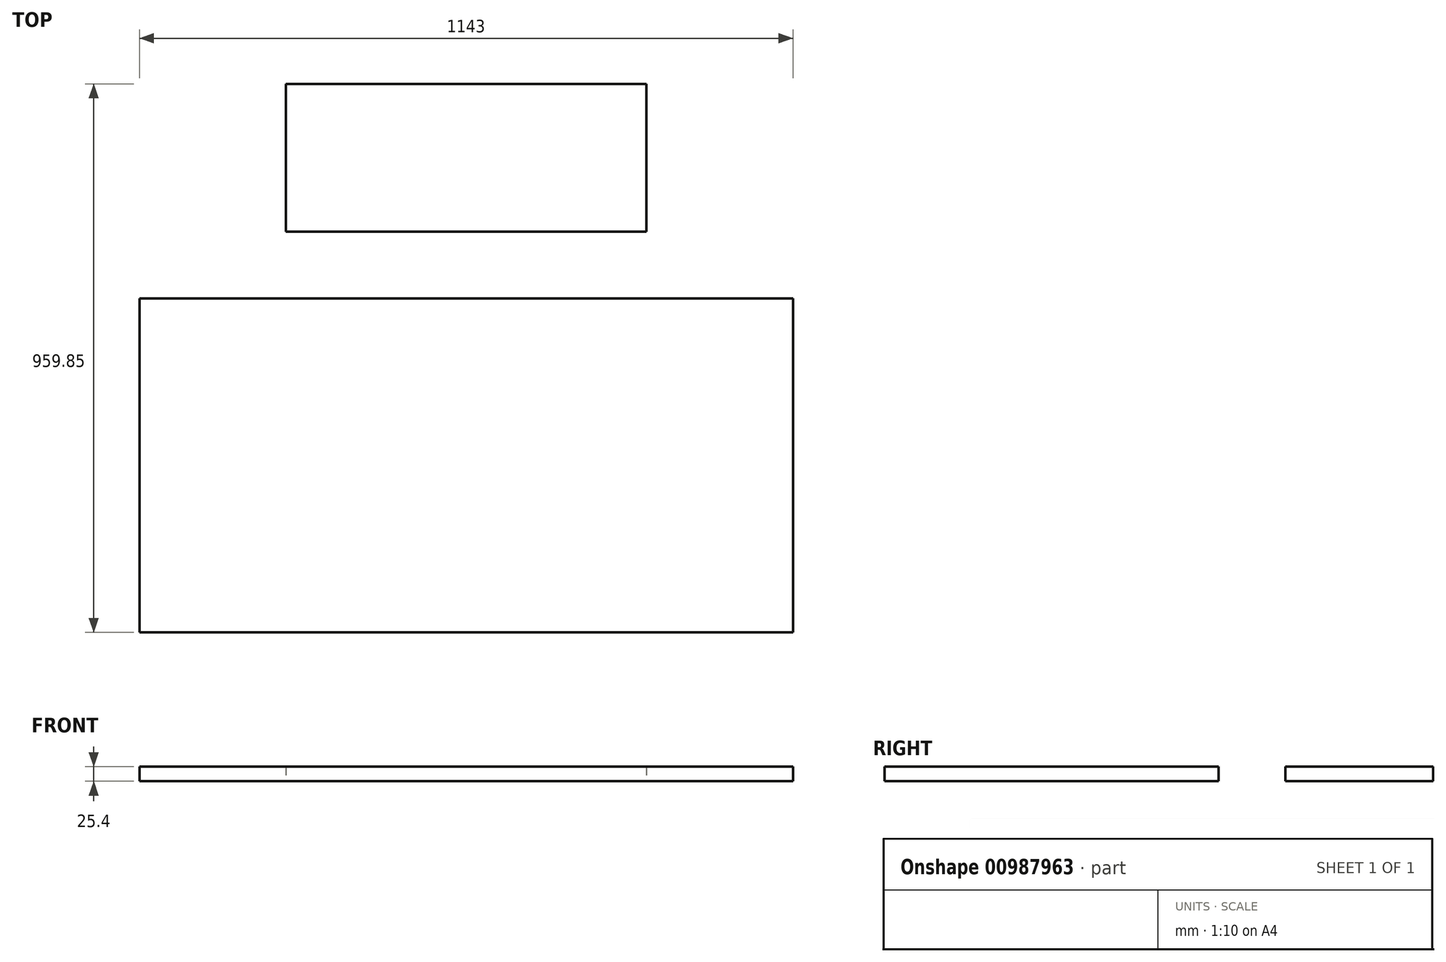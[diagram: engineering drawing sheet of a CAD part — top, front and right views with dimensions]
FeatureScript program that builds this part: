
annotation { "Feature Type Name" : "Feature", "Feature Type Description" : "" }
export const myFeature = defineFeature(function(context is Context, id is Id, definition is map)
    precondition{}
    {
        {
            var Q0;
            Q0=qCreatedBy(makeId("Top.planeOp"),FACE);
            var sketch = newSketch(context, id + "F0", { "sketchPlane" : qUnion([Q0])});
            skLineSegment(sketch, "E0.bottom", {"start": v(0, -44.7) * mm, "end": v(1143, -44.7) * mm});
            skLineSegment(sketch, "E0.top", {"start": v(0, 539.5) * mm, "end": v(1143, 539.5) * mm});
            skLineSegment(sketch, "E0.left", {"start": v(0, -44.7) * mm, "end": v(0, 539.5) * mm});
            skLineSegment(sketch, "E0.right", {"start": v(1143, -44.7) * mm, "end": v(1143, 539.5) * mm});
            skLineSegment(sketch, "E1.bottom", {"start": v(886.92, 915.14) * mm, "end": v(256.08, 915.14) * mm});
            skLineSegment(sketch, "E1.top", {"start": v(886.92, 656.58) * mm, "end": v(256.08, 656.58) * mm});
            skLineSegment(sketch, "E1.left", {"start": v(886.92, 915.14) * mm, "end": v(886.92, 656.58) * mm});
            skLineSegment(sketch, "E1.right", {"start": v(256.08, 915.14) * mm, "end": v(256.08, 656.58) * mm});
            skPoint(sketch, "E1.middle", {"position": v(571.5, 785.86) * mm});
            skPoint(sketch, "E1.middle.positionSnap0", {"position": v(571.5, 539.5) * mm});
            skPoint(sketch, "E1.centerSnap0", {"position": v(571.5, 539.5) * mm});
            skSolve(sketch);
        }
        {
            var Q0;
            Q0 = qSketchRegion(id + "F0", true);
            extrude(context, id + "F1", {"entities" : qUnion([Q0]), "depth" : 25.4 * mm, "offsetDistance" : 25.4 * mm});
        }
    });
